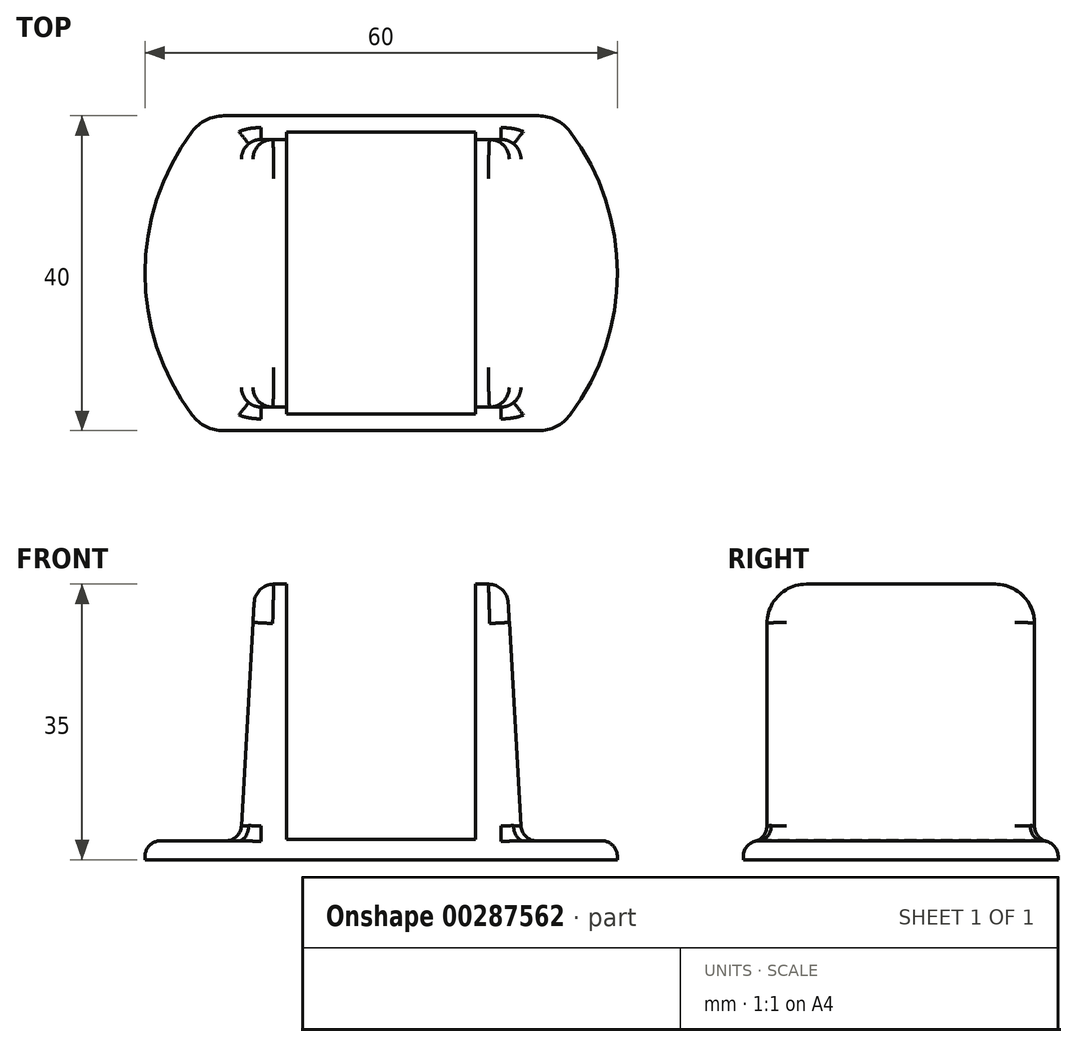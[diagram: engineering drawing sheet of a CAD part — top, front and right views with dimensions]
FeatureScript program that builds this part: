
annotation { "Feature Type Name" : "Feature", "Feature Type Description" : "" }
export const myFeature = defineFeature(function(context is Context, id is Id, definition is map)
    precondition{}
    {
        {
            var Q0;
            Q0=qCreatedBy(makeId("Front.planeOp"),FACE);
            var sketch = newSketch(context, id + "F0", { "sketchPlane" : qUnion([Q0])});
            skLineSegment(sketch, "E0", {"start": v(0, 0) * mm, "end": v(-12, 0) * mm});
            skLineSegment(sketch, "E1", {"start": v(-12, 2.6) * mm, "end": v(-12, 35) * mm});
            skLineSegment(sketch, "E2", {"start": v(-12, 35) * mm, "end": v(-16, 35) * mm});
            skLineSegment(sketch, "E3", {"start": v(0, 0) * mm, "end": v(0, 2.6) * mm});
            skLineSegment(sketch, "E4", {"start": v(0, 2.6) * mm, "end": v(-12, 2.6) * mm});
            skLineSegment(sketch, "E5", {"start": v(-12, 0) * mm, "end": v(-18, 0) * mm});
            skLineSegment(sketch, "E6", {"start": v(-18, 0) * mm, "end": v(-16, 35) * mm});
            skSolve(sketch);
        }
        {
            var Q0;
            Q0 = qSketchRegion(id + "F0", true);
            extrude(context, id + "F1", {"entities" : qUnion([Q0]), "endBound" : BoundingType.SYMMETRIC, "depth" : 34 * mm});
        }
        {
            var Q0;
            Q0=makeQuery(id+"F1.opExtrude","SWEPT_EDGE",EDGE,{"disambiguationData":[OSD([sQuery(id+"F0.wireOp",EDGE,"E2"),sQuery(id+"F0.wireOp",EDGE,"E6")])]});
            var Q1;
            Q1=makeQuery(id+"F1.opExtrude","CAP_EDGE",EDGE,{"disambiguationData":[OSD([sQuery(id+"F0.wireOp",EDGE,"E6")])],"isStart":false});
            var Q2;
            Q2=makeQuery(id+"F1.opExtrude","CAP_EDGE",EDGE,{"disambiguationData":[OSD([sQuery(id+"F0.wireOp",EDGE,"E6")])],"isStart":true});
            fillet(context, id + "F2", {"entities" : qUnion([Q0, Q1, Q2]), "radius" : 2.5 * mm, "tangentPropagation" : true, "allowEdgeOverflow" : false});
        }
        {
            var Q0;
            Q0=makeQuery(id+"F1.opExtrude","SWEPT_BODY",BODY,{"disambiguationData":[OSD([sQuery(id+"F0.wireOp",EDGE,"E0"),sQuery(id+"F0.wireOp",EDGE,"E1"),sQuery(id+"F0.wireOp",EDGE,"E2"),sQuery(id+"F0.wireOp",EDGE,"E3"),sQuery(id+"F0.wireOp",EDGE,"E4"),sQuery(id+"F0.wireOp",EDGE,"E5"),sQuery(id+"F0.wireOp",EDGE,"E6")])]});
            var Q1;
            Q1=qCreatedBy(makeId("Right.planeOp"),FACE);
            mirror(context, id + "F3", {"operationType" : NewBodyOperationType.ADD, "entities" : qUnion([Q0]), "mirrorPlane" : qUnion([Q1])});
        }
        {
            var Q0;
            Q0=qCreatedBy(makeId("Top.planeOp"),FACE);
            var sketch = newSketch(context, id + "F4", { "sketchPlane" : qUnion([Q0])});
            skArc(sketch, "E7", {"start": v(-22.36, 20) * mm, "mid": v(-30, 0) * mm, "end": v(-22.36, -20) * mm});
            skLineSegment(sketch, "E8", {"start": v(0, 0) * mm, "end": v(0, -20) * mm});
            skLineSegment(sketch, "E9", {"start": v(0, -20) * mm, "end": v(22.36, -20) * mm});
            skLineSegment(sketch, "E10", {"start": v(0, -20) * mm, "end": v(-22.36, -20) * mm});
            skLineSegment(sketch, "E11", {"start": v(0, 0) * mm, "end": v(0, 20) * mm});
            skLineSegment(sketch, "E12", {"start": v(0, 20) * mm, "end": v(22.36, 20) * mm});
            skLineSegment(sketch, "E13", {"start": v(0, 20) * mm, "end": v(-22.36, 20) * mm});
            skArc(sketch, "E14.trimOffspring", {"start": v(22.36, -20) * mm, "mid": v(30, 0) * mm, "end": v(22.36, 20) * mm});
            skSolve(sketch);
        }
        {
            var Q0;
            Q0 = qSketchRegion(id + "F4", true);
            extrude(context, id + "F5", {"entities" : qUnion([Q0]), "depth" : 2.4 * mm});
        }
        {
            var Q0;
            Q0=makeQuery(id+"F5.opExtrude","CAP_EDGE",EDGE,{"disambiguationData":[OSD([sQuery(id+"F4.wireOp",EDGE,"E7")])],"isStart":false});
            var Q1;
            Q1=makeQuery(id+"F5.opExtrude","CAP_EDGE",EDGE,{"disambiguationData":[OSD([sQuery(id+"F4.wireOp",EDGE,"E9"),sQuery(id+"F4.wireOp",EDGE,"E10")])],"isStart":false});
            var Q2;
            Q2=makeQuery(id+"F5.opExtrude","CAP_EDGE",EDGE,{"disambiguationData":[OSD([sQuery(id+"F4.wireOp",EDGE,"E14.trimOffspring")])],"isStart":false});
            var Q3;
            Q3=makeQuery(id+"F5.opExtrude","CAP_EDGE",EDGE,{"disambiguationData":[OSD([sQuery(id+"F4.wireOp",EDGE,"E12"),sQuery(id+"F4.wireOp",EDGE,"E13")])],"isStart":false});
            fillet(context, id + "F6", {"entities" : qUnion([Q0, Q1, Q2, Q3]), "radius" : 2 * mm, "tangentPropagation" : true, "allowEdgeOverflow" : false});
        }
        {
            var Q0;
            Q0=makeQuery(id+"F1.opExtrude","SWEPT_BODY",BODY,{"disambiguationData":[OSD([sQuery(id+"F0.wireOp",EDGE,"E0"),sQuery(id+"F0.wireOp",EDGE,"E1"),sQuery(id+"F0.wireOp",EDGE,"E2"),sQuery(id+"F0.wireOp",EDGE,"E3"),sQuery(id+"F0.wireOp",EDGE,"E4"),sQuery(id+"F0.wireOp",EDGE,"E5"),sQuery(id+"F0.wireOp",EDGE,"E6")])]});
            var Q1;
            Q1=makeQuery(id+"F5.opExtrude","SWEPT_BODY",BODY,{"disambiguationData":[OSD([sQuery(id+"F4.wireOp",EDGE,"E7"),sQuery(id+"F4.wireOp",EDGE,"E9"),sQuery(id+"F4.wireOp",EDGE,"E10"),sQuery(id+"F4.wireOp",EDGE,"E12"),sQuery(id+"F4.wireOp",EDGE,"E13"),sQuery(id+"F4.wireOp",EDGE,"E14.trimOffspring")])]});
            booleanBodies(context, id + "F7", {"operationType" : BooleanOperationType.UNION, "tools" : qUnion([Q0, Q1])});
        }
        {
            var Q0;
            {var subQ0=sQuery(id+"F0.wireOp",EDGE,"E6");Q0=makeQuery(id+"F2.opFillet","BLEND_EDGE",EDGE,{"blendedFrom":[makeQuery(id+"F1.opExtrude","SWEPT_EDGE",EDGE,{"disambiguationData":[OSD([sQuery(id+"F0.wireOp",EDGE,"E2"),subQ0])]}),makeQuery(id+"F1.opExtrude","CAP_EDGE",EDGE,{"disambiguationData":[OSD([subQ0])],"isStart":false})],"blendedInto":[]});}
            var Q1;
            {var subQ0=sQuery(id+"F0.wireOp",EDGE,"E6");Q1=makeQuery(id+"F2.opFillet","BLEND_EDGE",EDGE,{"blendedFrom":[makeQuery(id+"F1.opExtrude","SWEPT_EDGE",EDGE,{"disambiguationData":[OSD([sQuery(id+"F0.wireOp",EDGE,"E2"),subQ0])]}),makeQuery(id+"F1.opExtrude","CAP_EDGE",EDGE,{"disambiguationData":[OSD([subQ0])],"isStart":true})],"blendedInto":[]});}
            var Q2;
            {var subQ0=sQuery(id+"F0.wireOp",EDGE,"E6");Q2=makeQuery(id+"F3.opPattern","COPY",EDGE,{"derivedFrom":makeQuery(id+"F2.opFillet","BLEND_EDGE",EDGE,{"blendedFrom":[makeQuery(id+"F1.opExtrude","SWEPT_EDGE",EDGE,{"disambiguationData":[OSD([sQuery(id+"F0.wireOp",EDGE,"E2"),subQ0])]}),makeQuery(id+"F1.opExtrude","CAP_EDGE",EDGE,{"disambiguationData":[OSD([subQ0])],"isStart":false})],"blendedInto":[]}),"instanceName":"1"});}
            var Q3;
            {var subQ0=sQuery(id+"F0.wireOp",EDGE,"E6");Q3=makeQuery(id+"F3.opPattern","COPY",EDGE,{"derivedFrom":makeQuery(id+"F2.opFillet","BLEND_EDGE",EDGE,{"blendedFrom":[makeQuery(id+"F1.opExtrude","SWEPT_EDGE",EDGE,{"disambiguationData":[OSD([sQuery(id+"F0.wireOp",EDGE,"E2"),subQ0])]}),makeQuery(id+"F1.opExtrude","CAP_EDGE",EDGE,{"disambiguationData":[OSD([subQ0])],"isStart":true})],"blendedInto":[]}),"instanceName":"1"});}
            var Q4;
            Q4=makeQuery(id+"F6.opFillet","BLEND_EDGE",EDGE,{"blendedFrom":[makeQuery(id+"F5.opExtrude","CAP_EDGE",EDGE,{"disambiguationData":[OSD([sQuery(id+"F4.wireOp",EDGE,"E9"),sQuery(id+"F4.wireOp",EDGE,"E10")])],"isStart":false}),makeQuery(id+"F5.opExtrude","CAP_EDGE",EDGE,{"disambiguationData":[OSD([sQuery(id+"F4.wireOp",EDGE,"E14.trimOffspring")])],"isStart":false})],"blendedInto":[]});
            var Q5;
            Q5=makeQuery(id+"F6.opFillet","BLEND_EDGE",EDGE,{"blendedFrom":[makeQuery(id+"F5.opExtrude","CAP_EDGE",EDGE,{"disambiguationData":[OSD([sQuery(id+"F4.wireOp",EDGE,"E7")])],"isStart":false}),makeQuery(id+"F5.opExtrude","CAP_EDGE",EDGE,{"disambiguationData":[OSD([sQuery(id+"F4.wireOp",EDGE,"E9"),sQuery(id+"F4.wireOp",EDGE,"E10")])],"isStart":false})],"blendedInto":[]});
            var Q6;
            Q6=makeQuery(id+"F6.opFillet","BLEND_EDGE",EDGE,{"blendedFrom":[makeQuery(id+"F5.opExtrude","CAP_EDGE",EDGE,{"disambiguationData":[OSD([sQuery(id+"F4.wireOp",EDGE,"E7")])],"isStart":false}),makeQuery(id+"F5.opExtrude","CAP_EDGE",EDGE,{"disambiguationData":[OSD([sQuery(id+"F4.wireOp",EDGE,"E12"),sQuery(id+"F4.wireOp",EDGE,"E13")])],"isStart":false})],"blendedInto":[]});
            var Q7;
            Q7=makeQuery(id+"F6.opFillet","BLEND_EDGE",EDGE,{"blendedFrom":[makeQuery(id+"F5.opExtrude","CAP_EDGE",EDGE,{"disambiguationData":[OSD([sQuery(id+"F4.wireOp",EDGE,"E12"),sQuery(id+"F4.wireOp",EDGE,"E13")])],"isStart":false}),makeQuery(id+"F5.opExtrude","CAP_EDGE",EDGE,{"disambiguationData":[OSD([sQuery(id+"F4.wireOp",EDGE,"E14.trimOffspring")])],"isStart":false})],"blendedInto":[]});
            fillet(context, id + "F8", {"entities" : qUnion([Q0, Q1, Q2, Q3, Q4, Q5, Q6, Q7]), "radius" : 5 * mm, "tangentPropagation" : true, "allowEdgeOverflow" : false});
        }
        {
            var Q0;
            Q0=makeQuery(id+"F7.opBoolean","INTERSECT",EDGE,{"derivedFrom":[makeQuery(id+"F1.opExtrude","SWEPT_FACE",FACE,{"disambiguationData":[OSD([sQuery(id+"F0.wireOp",EDGE,"E6")])]}),makeQuery(id+"F5.opExtrude","CAP_FACE",FACE,{"disambiguationData":[OSD([sQuery(id+"F4.wireOp",EDGE,"E7"),sQuery(id+"F4.wireOp",EDGE,"E9"),sQuery(id+"F4.wireOp",EDGE,"E10"),sQuery(id+"F4.wireOp",EDGE,"E12"),sQuery(id+"F4.wireOp",EDGE,"E13"),sQuery(id+"F4.wireOp",EDGE,"E14.trimOffspring")])],"isStart":false})]});
            fillet(context, id + "F9", {"entities" : qUnion([Q0]), "radius" : 2 * mm, "tangentPropagation" : true, "allowEdgeOverflow" : false});
        }
    });
